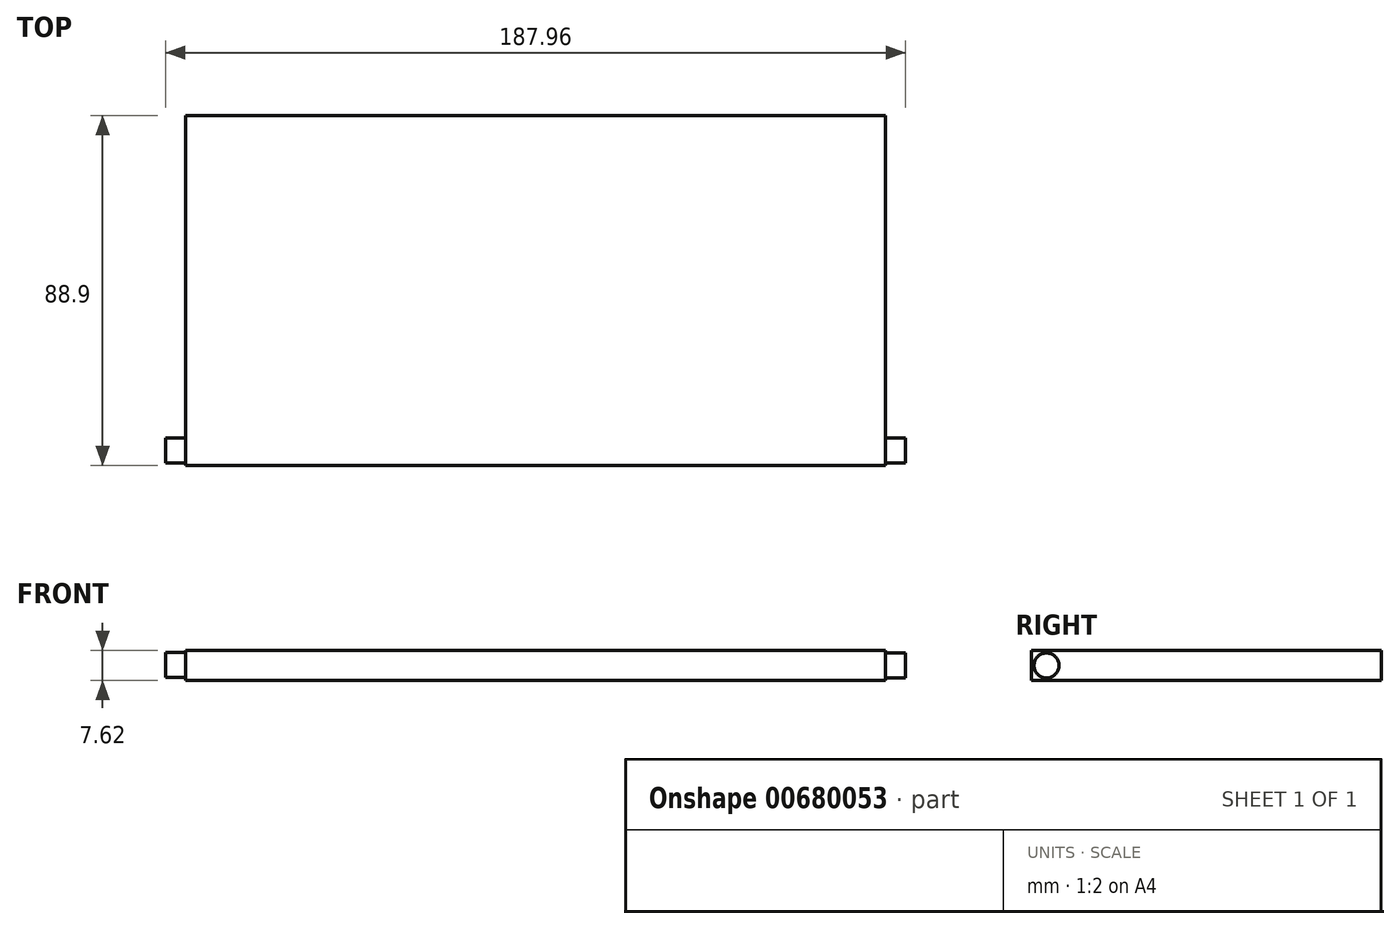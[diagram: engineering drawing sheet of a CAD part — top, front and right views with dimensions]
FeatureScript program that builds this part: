
annotation { "Feature Type Name" : "Feature", "Feature Type Description" : "" }
export const myFeature = defineFeature(function(context is Context, id is Id, definition is map)
    precondition{}
    {
        {
            var Q0;
            Q0=qCreatedBy(makeId("Top.planeOp"),FACE);
            var sketch = newSketch(context, id + "F0", { "sketchPlane" : qUnion([Q0])});
            skLineSegment(sketch, "E0.bottom", {"start": v(88.9, -44.45) * mm, "end": v(-88.9, -44.45) * mm});
            skLineSegment(sketch, "E0.top", {"start": v(88.9, 44.45) * mm, "end": v(-88.9, 44.45) * mm});
            skLineSegment(sketch, "E0.left", {"start": v(88.9, -44.45) * mm, "end": v(88.9, 44.45) * mm});
            skLineSegment(sketch, "E0.right", {"start": v(-88.9, -44.45) * mm, "end": v(-88.9, 44.45) * mm});
            skPoint(sketch, "E0.middle", {"position": v(0, 0) * mm});
            skSolve(sketch);
        }
        {
            var Q0;
            Q0 = qSketchRegion(id + "F0", true);
            extrude(context, id + "F1", {"entities" : qUnion([Q0]), "depth" : 7.62 * mm, "offsetDistance" : 25.4 * mm});
        }
        {
            var Q0;
            Q0=makeQuery(id+"F1.opExtrude","SWEPT_FACE",FACE,{"disambiguationData":[OSD([sQuery(id+"F0.wireOp",EDGE,"E0.right")])]});
            var sketch = newSketch(context, id + "F2", { "sketchPlane" : qUnion([Q0])});
            skCircle(sketch, "E1", {"center": v(40.64, 3.94) * mm, "radius": 3.18 * mm});
            skSolve(sketch);
        }
        {
            var Q0;
            Q0 = qSketchRegion(id + "F2", true);
            extrude(context, id + "F3", {"entities" : qUnion([Q0]), "operationType" : NewBodyOperationType.ADD, "depth" : 5.08 * mm, "offsetDistance" : 25.4 * mm});
        }
        {
            var Q0;
            Q0=makeQuery(id+"F1.opExtrude","SWEPT_FACE",FACE,{"disambiguationData":[OSD([sQuery(id+"F0.wireOp",EDGE,"E0.left")])]});
            var sketch = newSketch(context, id + "F4", { "sketchPlane" : qUnion([Q0])});
            skCircle(sketch, "E2", {"center": v(-40.62, 3.8) * mm, "radius": 3.18 * mm});
            skSolve(sketch);
        }
        {
            var Q0;
            Q0 = qSketchRegion(id + "F4", true);
            extrude(context, id + "F5", {"entities" : qUnion([Q0]), "operationType" : NewBodyOperationType.ADD, "depth" : 5.08 * mm, "offsetDistance" : 25.4 * mm});
        }
    });
